# Revit family: Festpunktkonsole 120- 55
name_source: partatom
category: HLS-Bauteile
revit_build: Autodesk Revit 2017 (Build: 20190507_1515(x64)
units: mm (PartAtom-declared; Revit-internal decimal feet)

## family parameters
Basisbauteil = Fläche
Beim Laden mit Abzugskörper schneiden = Nein
Bemaßung runder Anschluss = Durchmesser verwenden
Gemeinsam genutzt = Ja
Raumberechnungspunkt = Nein
Teiletyp = Normal

## types (7) — shared parameters
Artikelnummer = 9996491
Breite Platte = 200 mm  [stored 0.656168 ft]
Breite Profil = 120 mm  [stored 0.393701 ft]
EAN = 4250928446923
Fabrikat = MEFA
Firma = MEFA Befestigungs- und Montagesysteme GmbH
Gewicht = 13.60 kg
Gewicht pro Bauteil = 13.60 kg
Höhe Profil = 55 mm  [stored 0.180446 ft]
Kurztext1 = Festpunktkonsole U-Profil 120/55
Kurztext2 = L= 750 mm Platte blank
Langloch Platte = 14x27 mm
Lochabstand = 150 mm
Lochdurchmesser = 14 mm
Länge Konsole = 750 mm
Länge Platte = 200 mm  [stored 0.656168 ft]
Material = Stahl
Materialname C-Profil = S235JR
Materialname Platte = S235JR
Oberflaeche = blank
Profil = U-Profil
S = 10 mm  [stored 0.0328084 ft]
Stärke Platte = 10 mm  [stored 0.0328084 ft]
Vorgabe-Ansicht = 1219 mm
für Rohrdurchmesser = ab 60 mm
max. zul. Last F1 = 0.00 kip
max. zul. Last F2 = 0.00 kip
max. zul. Last q0 = 0.000 kip/ft
zero-valued in all types: Stärke Profil

## per-type parameters (varying)
| type | Länge U-Stahl |
| Festpunktkonsole 120/55, L=100 | U-Stahl 120-55-100 bis 700 : U-Stahl 120x55x100 |
| Festpunktkonsole 120/55, L=200 | U-Stahl 120-55-100 bis 700 : U-Stahl 120x55x200 |
| Festpunktkonsole 120/55, L=300 | U-Stahl 120-55-100 bis 700 : U-Stahl 120x55x300 |
| Festpunktkonsole 120/55, L=400 | U-Stahl 120-55-100 bis 700 : U-Stahl 120x55x400 |
| Festpunktkonsole 120/55, L=500 | U-Stahl 120-55-100 bis 700 : U-Stahl 120x55x500 |
| Festpunktkonsole 120/55, L=600 | U-Stahl 120-55-100 bis 700 : U-Stahl 120x55x600 |
| Festpunktkonsole 120/55, L=700 | U-Stahl 120-55-100 bis 700 : U-Stahl 120x55x700 |

note: [stored X ft] marks values corroborated as IEEE doubles in the binary element streams (Revit-internal decimal feet)
